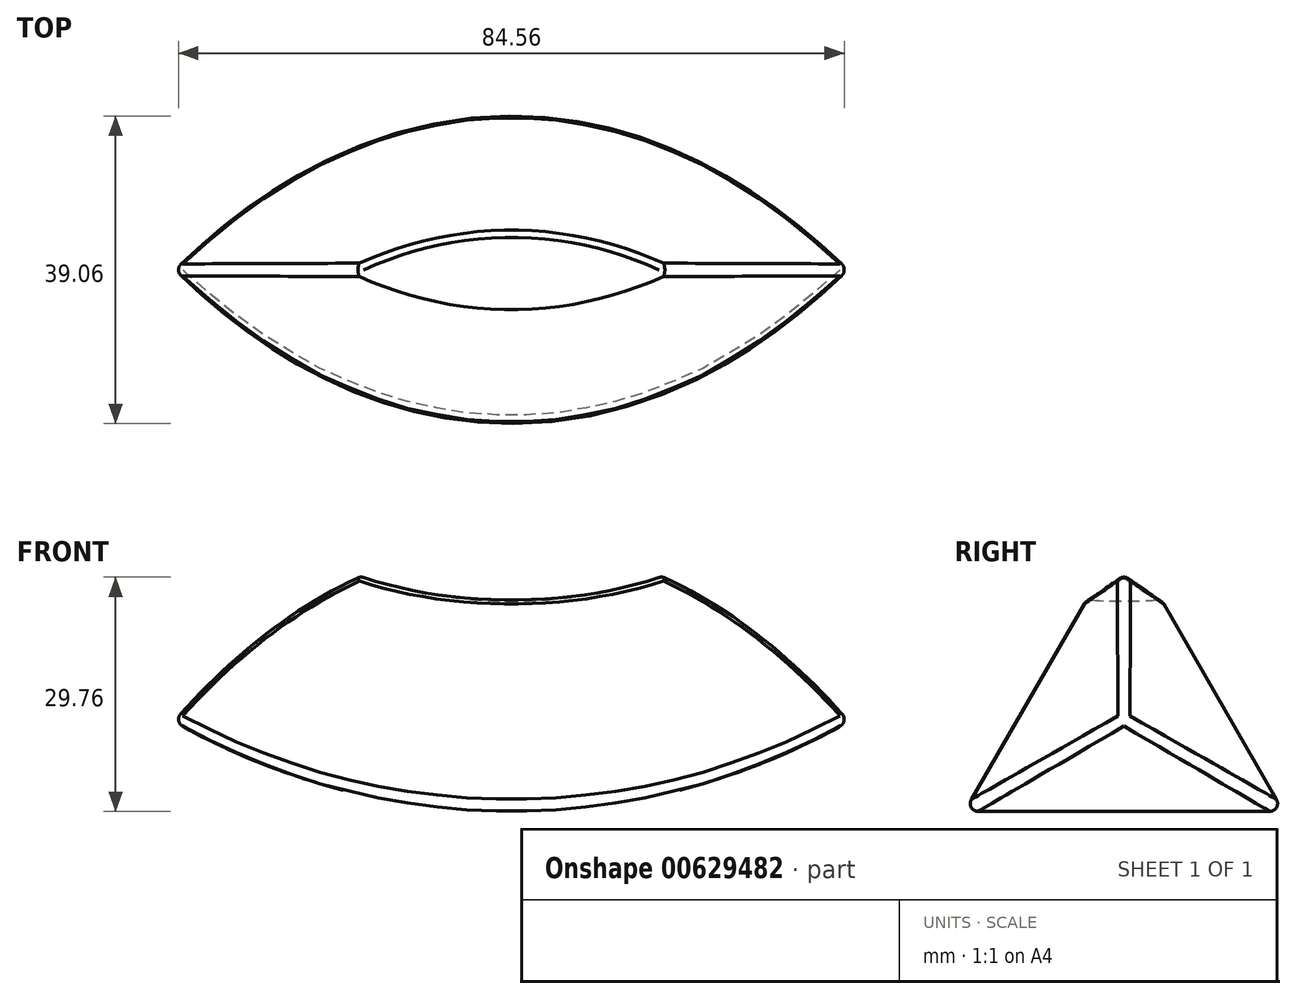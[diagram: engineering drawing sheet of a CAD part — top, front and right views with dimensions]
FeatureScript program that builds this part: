
annotation { "Feature Type Name" : "Feature", "Feature Type Description" : "" }
export const myFeature = defineFeature(function(context is Context, id is Id, definition is map)
    precondition{}
    {
        {
            var Q0;
            Q0=qCreatedBy(makeId("Right.planeOp"),FACE);
            var sketch = newSketch(context, id + "F0", { "sketchPlane" : qUnion([Q0])});
            skCircle(sketch, "E0.cCircle", {"center": v(0, 25) * mm, "radius": 25 * mm, "construction": true});
            skLineSegment(sketch, "E0.0", {"start": v(0, 75) * mm, "end": v(43.3, 0) * mm});
            skLineSegment(sketch, "E0.1", {"start": v(43.3, 0) * mm, "end": v(-43.3, 0) * mm});
            skLineSegment(sketch, "E0.2", {"start": v(-43.3, 0) * mm, "end": v(0, 75) * mm});
            skPoint(sketch, "E0.0.midPoint", {"position": v(21.65, 37.5) * mm});
            skSolve(sketch);
        }
        {
            var Q0;
            Q0=makeQuery(id+"F0.imprint","IMPRINT",FACE,{"disambiguationData":[TD([[makeQuery(id+"F0.imprint","IMPRINT",EDGE,{"derivedFrom":sQuery(id+"F0.wireOp",EDGE,"E0.0")}),-1.0]])]});
            extrude(context, id + "F1", {"entities" : qUnion([Q0]), "depth" : 50 * mm, "offsetDistance" : 25 * mm, "hasDraft" : true, "draftAngle" : 30 * degree, "draftPullDirection" : true});
        }
        {
            var Q0;
            Q0=makeQuery(id+"F1.opExtrude","CAP_FACE",FACE,{"disambiguationData":[OSD([sQuery(id+"F0.wireOp",EDGE,"E0.0"),sQuery(id+"F0.wireOp",EDGE,"E0.1"),sQuery(id+"F0.wireOp",EDGE,"E0.2")])],"isStart":true});
            extrude(context, id + "F2", {"entities" : qUnion([Q0]), "operationType" : NewBodyOperationType.ADD, "depth" : 50 * mm, "offsetDistance" : 25 * mm, "hasDraft" : true, "draftAngle" : 30 * degree, "draftPullDirection" : true});
        }
        {
            var Q0;
            {var subQ0=sQuery(id+"F0.wireOp",EDGE,"E0.1");Q0=makeQuery(id+"F2.boolean.opBoolean","MERGE",EDGE,{"derivedFrom":[makeQuery(id+"F1.opExtrude","CAP_EDGE",EDGE,{"disambiguationData":[OSD([subQ0])],"isStart":true}),makeQuery(id+"F2.opExtrude","CAP_EDGE",EDGE,{"disambiguationData":[OSD([subQ0])],"isStart":true})]});}
            var Q1;
            {var subQ0=sQuery(id+"F0.wireOp",EDGE,"E0.2");Q1=makeQuery(id+"F2.boolean.opBoolean","MERGE",EDGE,{"derivedFrom":[makeQuery(id+"F1.opExtrude","CAP_EDGE",EDGE,{"disambiguationData":[OSD([subQ0])],"isStart":true}),makeQuery(id+"F2.opExtrude","CAP_EDGE",EDGE,{"disambiguationData":[OSD([subQ0])],"isStart":true})]});}
            var Q2;
            {var subQ0=sQuery(id+"F0.wireOp",EDGE,"E0.0");Q2=makeQuery(id+"F2.boolean.opBoolean","MERGE",EDGE,{"derivedFrom":[makeQuery(id+"F1.opExtrude","CAP_EDGE",EDGE,{"disambiguationData":[OSD([subQ0])],"isStart":true}),makeQuery(id+"F2.opExtrude","CAP_EDGE",EDGE,{"disambiguationData":[OSD([subQ0])],"isStart":true})]});}
            fillet(context, id + "F3", {"entities" : qUnion([Q0, Q1, Q2]), "radius" : 86 * mm, "allowEdgeOverflow" : false});
        }
        {
            var Q0;
            Q0=qCreatedBy(makeId("Front.planeOp"),FACE);
            var sketch = newSketch(context, id + "F4", { "sketchPlane" : qUnion([Q0])});
            skArc(sketch, "E1", {"start": v(-37.5, 53.16) * mm, "mid": v(0, 40) * mm, "end": v(37.5, 53.16) * mm});
            skLineSegment(sketch, "E2", {"start": v(-37.5, 53.16) * mm, "end": v(37.5, 53.16) * mm});
            skLineSegment(sketch, "E3", {"start": v(0, 100) * mm, "end": v(-49.77, 100) * mm, "construction": true});
            skSolve(sketch);
        }
        {
            var Q0;
            Q0=makeQuery(id+"F4.imprint","IMPRINT",FACE,{"disambiguationData":[TD([[makeQuery(id+"F4.imprint","IMPRINT",EDGE,{"derivedFrom":sQuery(id+"F4.wireOp",EDGE,"E1")}),1.0]])]});
            var Q1;
            Q1=sQuery(id+"F4.wireOp",EDGE,"E3");
            revolve(context, id + "F5", {"operationType" : NewBodyOperationType.REMOVE, "entities" : qUnion([Q0]), "axis" : qUnion([Q1]), "revolveType" : RevolveType.FULL, "oppositeDirection" : true});
        }
        {
            var Q0;
            Q0=qCreatedBy(makeId("Front.planeOp"),FACE);
            var sketch = newSketch(context, id + "F6", { "sketchPlane" : qUnion([Q0])});
            skPoint(sketch, "E4.0", {"position": v(43.3, 25) * mm});
            skPoint(sketch, "E5.0", {"position": v(-43.3, 25) * mm});
            skLineSegment(sketch, "E6", {"start": v(-43.3, 25) * mm, "end": v(43.3, 25) * mm});
            skSolve(sketch);
        }
        {
            var Q0;
            Q0=makeQuery(id+"F3.opFillet","BLEND_FACE",FACE,{"disambiguationData":[OSD([sQuery(id+"F0.wireOp",EDGE,"E0.2")])]});
            var Q1;
            Q1=makeQuery(id+"F3.opFillet","BLEND_FACE",FACE,{"disambiguationData":[OSD([sQuery(id+"F0.wireOp",EDGE,"E0.0")])]});
            var Q2;
            Q2=makeQuery(id+"F3.opFillet","BLEND_FACE",FACE,{"disambiguationData":[OSD([sQuery(id+"F0.wireOp",EDGE,"E0.1")])]});
            fillet(context, id + "F7", {"entities" : qUnion([Q0, Q1, Q2]), "radius" : 1 * mm, "tangentPropagation" : true, "allowEdgeOverflow" : false});
        }
    });
